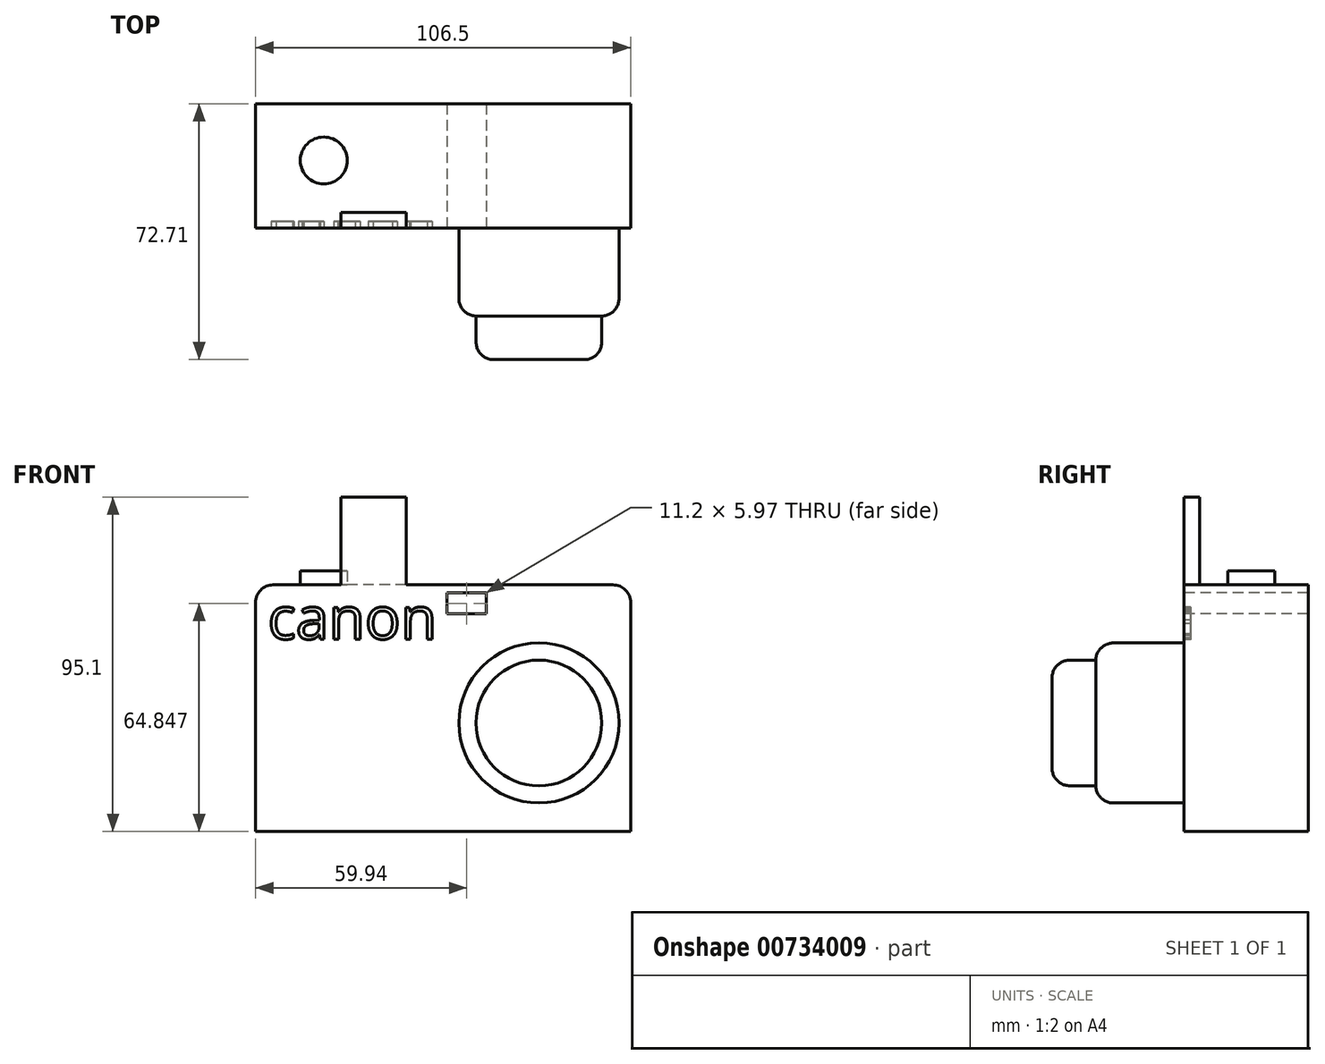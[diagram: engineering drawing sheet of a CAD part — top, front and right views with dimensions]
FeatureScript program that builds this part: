
annotation { "Feature Type Name" : "Feature", "Feature Type Description" : "" }
export const myFeature = defineFeature(function(context is Context, id is Id, definition is map)
    precondition{}
    {
        {
            var Q0;
            Q0=qCreatedBy(makeId("Top.planeOp"),FACE);
            var sketch = newSketch(context, id + "F0", { "sketchPlane" : qUnion([Q0])});
            skLineSegment(sketch, "E0.bottom", {"start": v(-149.57, 40.82) * mm, "end": v(-43.07, 40.82) * mm});
            skLineSegment(sketch, "E0.top", {"start": v(-149.57, 5.5) * mm, "end": v(-43.07, 5.5) * mm});
            skLineSegment(sketch, "E0.left", {"start": v(-149.57, 40.82) * mm, "end": v(-149.57, 5.5) * mm});
            skLineSegment(sketch, "E0.right", {"start": v(-43.07, 40.82) * mm, "end": v(-43.07, 5.5) * mm});
            skSolve(sketch);
        }
        {
            var Q0;
            Q0 = qSketchRegion(id + "F0", true);
            extrude(context, id + "F1", {"entities" : qUnion([Q0]), "depth" : 70.1 * mm, "offsetDistance" : 25 * mm});
        }
        {
            var Q0;
            Q0=makeQuery(id+"F1.opExtrude","SWEPT_FACE",FACE,{"disambiguationData":[OSD([sQuery(id+"F0.wireOp",EDGE,"E0.top")])]});
            var sketch = newSketch(context, id + "F2", { "sketchPlane" : qUnion([Q0])});
            skCircle(sketch, "E1", {"center": v(-69.1, 30.87) * mm, "radius": 22.73 * mm});
            skSolve(sketch);
        }
        {
            var Q0;
            Q0 = qSketchRegion(id + "F2", true);
            extrude(context, id + "F3", {"entities" : qUnion([Q0]), "operationType" : NewBodyOperationType.ADD, "depth" : 25 * mm, "offsetDistance" : 25 * mm});
        }
        {
            var Q0;
            Q0=makeQuery(id+"F3.opExtrude","CAP_FACE",FACE,{"disambiguationData":[OSD([sQuery(id+"F2.wireOp",EDGE,"E1")])],"isStart":false});
            var sketch = newSketch(context, id + "F4", { "sketchPlane" : qUnion([Q0])});
            skCircle(sketch, "E2", {"center": v(-69.1, 30.87) * mm, "radius": 17.5 * mm});
            skSolve(sketch);
        }
        {
            var Q0;
            Q0 = qSketchRegion(id + "F4", true);
            extrude(context, id + "F5", {"entities" : qUnion([Q0]), "operationType" : NewBodyOperationType.ADD, "oppositeDirection" : true, "depth" : 9.4 * mm, "offsetDistance" : 25 * mm});
        }
        {
            var Q0;
            Q0=makeQuery(id+"F3.opExtrude","CAP_FACE",FACE,{"disambiguationData":[OSD([sQuery(id+"F2.wireOp",EDGE,"E1")])],"isStart":false});
            var sketch = newSketch(context, id + "F6", { "sketchPlane" : qUnion([Q0])});
            skCircle(sketch, "E3", {"center": v(-69.1, 30.87) * mm, "radius": 17.85 * mm});
            skSolve(sketch);
        }
        {
            var Q0;
            Q0=makeQuery(id+"F6.imprint","IMPRINT",FACE,{"disambiguationData":[TD([[makeQuery(id+"F6.imprint","IMPRINT",EDGE,{"derivedFrom":sQuery(id+"F6.wireOp",EDGE,"E3")}),1.0]])]});
            extrude(context, id + "F7", {"entities" : qUnion([Q0]), "operationType" : NewBodyOperationType.ADD, "depth" : 12.4 * mm, "offsetDistance" : 25 * mm});
        }
        {
            var Q0;
            Q0=makeQuery(id+"F1.opExtrude","CAP_EDGE",EDGE,{"disambiguationData":[OSD([sQuery(id+"F0.wireOp",EDGE,"E0.right")])],"isStart":false});
            var Q1;
            Q1=makeQuery(id+"F1.opExtrude","CAP_EDGE",EDGE,{"disambiguationData":[OSD([sQuery(id+"F0.wireOp",EDGE,"E0.left")])],"isStart":false});
            var Q2;
            Q2=makeQuery(id+"F7.opExtrude","CAP_EDGE",EDGE,{"disambiguationData":[OSD([sQuery(id+"F6.wireOp",EDGE,"E3")])],"isStart":false});
            var Q3;
            Q3=makeQuery(id+"F3.opExtrude","CAP_EDGE",EDGE,{"disambiguationData":[OSD([sQuery(id+"F2.wireOp",EDGE,"E1")])],"isStart":false});
            fillet(context, id + "F8", {"entities" : qUnion([Q0, Q1, Q2, Q3]), "radius" : 5 * mm, "tangentPropagation" : true, "allowEdgeOverflow" : false});
        }
        {
            var Q0;
            Q0=makeQuery(id+"F1.opExtrude","CAP_FACE",FACE,{"disambiguationData":[OSD([sQuery(id+"F0.wireOp",EDGE,"E0.bottom"),sQuery(id+"F0.wireOp",EDGE,"E0.top"),sQuery(id+"F0.wireOp",EDGE,"E0.left"),sQuery(id+"F0.wireOp",EDGE,"E0.right")])],"isStart":false});
            var sketch = newSketch(context, id + "F9", { "sketchPlane" : qUnion([Q0])});
            skCircle(sketch, "E4", {"center": v(-130.18, 24.7) * mm, "radius": 6.67 * mm});
            skSolve(sketch);
        }
        {
            var Q0;
            Q0 = qSketchRegion(id + "F9", true);
            extrude(context, id + "F10", {"entities" : qUnion([Q0]), "operationType" : NewBodyOperationType.ADD, "depth" : 4 * mm, "offsetDistance" : 25 * mm});
        }
        {
            var Q0;
            Q0=makeQuery(id+"F1.opExtrude","SWEPT_FACE",FACE,{"disambiguationData":[OSD([sQuery(id+"F0.wireOp",EDGE,"E0.top")])]});
            var sketch = newSketch(context, id + "F11", { "sketchPlane" : qUnion([Q0])});
            skText(sketch, "E5", { "text": "canon", "fontName": "OpenSans-Regular.ttf"});
            const initialGuessF11  = {"E5": [-0.14609, 0.05471, 1, 0, 0.01206]};
            skSetInitialGuess(sketch, initialGuessF11);
            skSolve(sketch);
        }
        {
            var Q0;
            Q0 = qSketchRegion(id + "F11", true);
            extrude(context, id + "F12", {"entities" : qUnion([Q0]), "operationType" : NewBodyOperationType.REMOVE, "oppositeDirection" : true, "depth" : 1.9 * mm, "offsetDistance" : 25 * mm});
        }
        {
            var Q0;
            {var subQ0=sQuery(id+"F0.wireOp",EDGE,"E0.left");var subQ2=sQuery(id+"F0.wireOp",EDGE,"E0.top");Q0=makeQuery(id+"F12.boolean.opBoolean","SPLIT",FACE,{"disambiguationData":[TD([makeQuery(id+"F1.opExtrude","SWEPT_FACE",FACE,{"disambiguationData":[OSD([subQ0])]})])],"derivedFrom":makeQuery(id+"F1.opExtrude","SWEPT_FACE",FACE,{"disambiguationData":[OSD([subQ2])]})});}
            var sketch = newSketch(context, id + "F13", { "sketchPlane" : qUnion([Q0])});
            skLineSegment(sketch, "E6.bottom", {"start": v(-95.23, 67.83) * mm, "end": v(-84.03, 67.83) * mm});
            skLineSegment(sketch, "E6.top", {"start": v(-95.23, 61.86) * mm, "end": v(-84.03, 61.86) * mm});
            skLineSegment(sketch, "E6.left", {"start": v(-95.23, 67.83) * mm, "end": v(-95.23, 61.86) * mm});
            skLineSegment(sketch, "E6.right", {"start": v(-84.03, 67.83) * mm, "end": v(-84.03, 61.86) * mm});
            skSolve(sketch);
        }
        {
            var Q0;
            Q0 = qSketchRegion(id + "F13", true);
            extrude(context, id + "F14", {"entities" : qUnion([Q0]), "operationType" : NewBodyOperationType.REMOVE, "oppositeDirection" : true, "depth" : 57.4 * mm, "offsetDistance" : 25 * mm});
        }
        {
            var Q0;
            {var subQ0=sQuery(id+"F0.wireOp",EDGE,"E0.left");var subQ2=sQuery(id+"F0.wireOp",EDGE,"E0.top");Q0=makeQuery(id+"F12.boolean.opBoolean","SPLIT",FACE,{"disambiguationData":[TD([makeQuery(id+"F1.opExtrude","SWEPT_FACE",FACE,{"disambiguationData":[OSD([subQ0])]})])],"derivedFrom":makeQuery(id+"F1.opExtrude","SWEPT_FACE",FACE,{"disambiguationData":[OSD([subQ2])]})});}
            var sketch = newSketch(context, id + "F15", { "sketchPlane" : qUnion([Q0])});
            skLineSegment(sketch, "E7.bottom", {"start": v(-149.57, 42.02) * mm, "end": v(-94.52, 42.02) * mm});
            skLineSegment(sketch, "E7.top", {"start": v(-149.57, 3.63) * mm, "end": v(-94.52, 3.63) * mm});
            skLineSegment(sketch, "E7.left", {"start": v(-149.57, 42.02) * mm, "end": v(-149.57, 3.63) * mm});
            skLineSegment(sketch, "E7.right", {"start": v(-94.52, 42.02) * mm, "end": v(-94.52, 3.63) * mm});
            skLineSegment(sketch, "E8.bottom", {"start": v(-94.52, 3.63) * mm, "end": v(-146.97, 3.63) * mm});
            skLineSegment(sketch, "E8.top", {"start": v(-94.52, 42.02) * mm, "end": v(-146.97, 42.02) * mm});
            skLineSegment(sketch, "E8.left", {"start": v(-94.52, 3.63) * mm, "end": v(-94.52, 42.02) * mm});
            skLineSegment(sketch, "E8.right", {"start": v(-146.97, 3.63) * mm, "end": v(-146.97, 42.02) * mm});
            skSolve(sketch);
        }
        {
            var Q0;
            Q0=makeQuery(id+"F1.opExtrude","CAP_FACE",FACE,{"disambiguationData":[OSD([sQuery(id+"F0.wireOp",EDGE,"E0.bottom"),sQuery(id+"F0.wireOp",EDGE,"E0.top"),sQuery(id+"F0.wireOp",EDGE,"E0.left"),sQuery(id+"F0.wireOp",EDGE,"E0.right")])],"isStart":false});
            var sketch = newSketch(context, id + "F16", { "sketchPlane" : qUnion([Q0])});
            skLineSegment(sketch, "E9.bottom", {"start": v(-106.8, 9.98) * mm, "end": v(-125.27, 9.98) * mm});
            skLineSegment(sketch, "E9.top", {"start": v(-106.8, 5.5) * mm, "end": v(-125.27, 5.5) * mm});
            skLineSegment(sketch, "E9.left", {"start": v(-106.8, 9.98) * mm, "end": v(-106.8, 5.5) * mm});
            skLineSegment(sketch, "E9.right", {"start": v(-125.27, 9.98) * mm, "end": v(-125.27, 5.5) * mm});
            skSolve(sketch);
        }
        {
            var Q0;
            Q0 = qSketchRegion(id + "F16", true);
            extrude(context, id + "F17", {"entities" : qUnion([Q0]), "operationType" : NewBodyOperationType.ADD, "depth" : 25 * mm, "offsetDistance" : 25 * mm});
        }
    });
